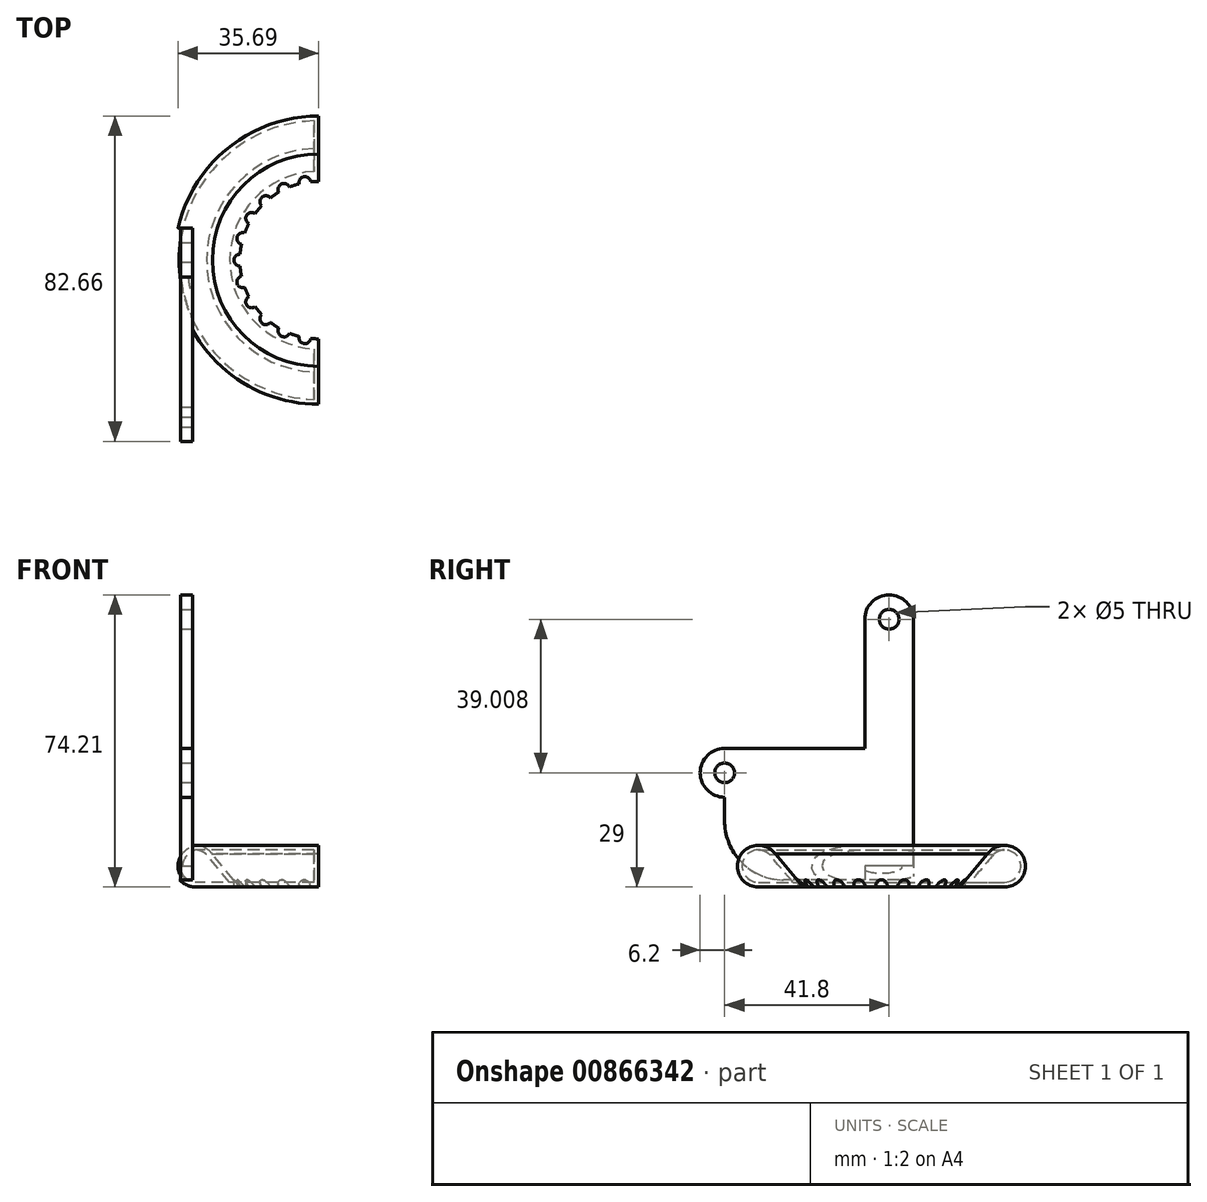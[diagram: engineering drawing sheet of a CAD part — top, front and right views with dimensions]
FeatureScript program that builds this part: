
annotation { "Feature Type Name" : "Feature", "Feature Type Description" : "" }
export const myFeature = defineFeature(function(context is Context, id is Id, definition is map)
    precondition{}
    {
        {
            var Q0;
            Q0=qCreatedBy(makeId("Front.planeOp"),FACE);
            var sketch = newSketch(context, id + "F0", { "sketchPlane" : qUnion([Q0])});
            skArc(sketch, "E0", {"start": v(-28.43, 2.91) * mm, "mid": v(-35.1, 1.56) * mm, "end": v(-31.3, -4.1) * mm});
            skLineSegment(sketch, "E1", {"start": v(-31.3, -4.1) * mm, "end": v(-31.3, -4.1) * mm});
            skLineSegment(sketch, "E2", {"start": v(-31.3, -4.1) * mm, "end": v(-22.57, -4.1) * mm});
            skLineSegment(sketch, "E3", {"start": v(-22.57, -4.1) * mm, "end": v(-28.43, 2.91) * mm});
            skArc(sketch, "E4.0", {"start": v(-26.94, 3) * mm, "mid": v(-36, 2.47) * mm, "end": v(-31.3, -5.3) * mm});
            skLineSegment(sketch, "E5.0", {"start": v(-20, -5.3) * mm, "end": v(-26.97, 3.05) * mm});
            skLineSegment(sketch, "E5.1", {"start": v(-31.3, -5.3) * mm, "end": v(-20, -5.3) * mm});
            skSolve(sketch);
        }
        {
            var Q0;
            Q0=qCreatedBy(makeId("Top.planeOp"),FACE);
            var sketch = newSketch(context, id + "F1", { "sketchPlane" : qUnion([Q0])});
            skCircle(sketch, "E6", {"center": v(0, 0) * mm, "radius": 20 * mm, "construction": true});
            skSolve(sketch);
        }
        {
            var Q0;
            {var subQ3=sQuery(id+"F0.wireOp",EDGE,"E2");Q0=makeQuery(id+"F0.imprint","IMPRINT",FACE,{"disambiguationData":[TD([[makeQuery(id+"F0.imprint","IMPRINT",EDGE,{"derivedFrom":subQ3}),-1.0]])]});}
            var Q1;
            Q1=sQuery(id+"F1.wireOp",EDGE,"E6");
            revolve(context, id + "F2", {"surfaceOperationType" : NewSurfaceOperationType.NEW, "entities" : qUnion([Q0]), "axis" : qUnion([Q1]), "revolveType" : RevolveType.SYMMETRIC, "angle" : 180 * degree});
        }
        {
            var Q0;
            Q0=qCreatedBy(makeId("Top.planeOp"),FACE);
            cPlane(context, id + "F3", {"entities" : qUnion([Q0]), "cplaneType" : CPlaneType.OFFSET, "offset" : 7 * mm, "width" : 150 * mm, "height" : 150 * mm});
        }
        {
            var Q0;
            Q0=qCreatedBy(id+"F3.planeOp",FACE);
            var sketch = newSketch(context, id + "F4", { "sketchPlane" : qUnion([Q0])});
            skCircle(sketch, "E7", {"center": v(-20.03, 0) * mm, "radius": 1.5 * mm});
            skSolve(sketch);
        }
        {
            var Q0;
            Q0=makeQuery(id+"F4.imprint","IMPRINT",FACE,{"disambiguationData":[TD([[makeQuery(id+"F4.imprint","IMPRINT",EDGE,{"derivedFrom":sQuery(id+"F4.wireOp",EDGE,"86y424w5-kA8f-6XOt-aXa2-UrsFHTbOcK4u")}),-1.0]])]});
            var Q1;
            Q1=makeQuery(id+"F4.imprint","IMPRINT",FACE,{"disambiguationData":[TD([[makeQuery(id+"F4.imprint","IMPRINT",EDGE,{"derivedFrom":sQuery(id+"F4.wireOp",EDGE,"E7")}),1.0]])]});
            var Q2;
            Q2=sQuery(id+"F4.wireOp",EDGE,"RAvej1WS-v9vJ-C49S-39A3-zDTatcSTJvx6");
            var Q3;
            Q3=sQuery(id+"F4.wireOp",EDGE,"86y424w5-kA8f-6XOt-aXa2-UrsFHTbOcK4u");
            var Q4;
            Q4=sQuery(id+"F4.wireOp",EDGE,"Bvj7dinE-6FqB-1OQW-Px6F-VovOO4BtMCvj");
            var Q5;
            Q5=makeQuery(id+"F2.opRevolve","SWEPT_FACE",FACE,{"disambiguationData":[OSD([sQuery(id+"F0.wireOp",EDGE,"E5.1")])]});
            extrude(context, id + "F5", {"entities" : qUnion([Q0, Q1]), "surfaceEntities" : qUnion([Q2, Q3, Q4]), "oppositeDirection" : true, "depth" : 20 * mm, "endBoundEntityFace" : qUnion([Q5]), "offsetDistance" : 25 * mm, "hasDraft" : true, "draftAngle" : 0 * degree});
        }
        {
            var Q0;
            Q0=makeQuery(id+"F5.opExtrude","SWEPT_BODY",BODY,{"disambiguationData":[OSD([sQuery(id+"F4.wireOp",EDGE,"E7")])]});
            var Q1;
            Q1=makeQuery(id+"F2.opRevolve","SWEPT_FACE",FACE,{"disambiguationData":[OSD([sQuery(id+"F0.wireOp",EDGE,"E5.0")])]});
            circularPattern(context, id + "F6", {"operationType" : NewBodyOperationType.REMOVE, "entities" : qUnion([Q0]), "axis" : qUnion([Q1]), "angle" : 160 * degree, "instanceCount" : 11, "equalSpace" : true, "isCentered" : true});
        }
        {
            var Q0;
            Q0=qCreatedBy(makeId("Right.planeOp"),FACE);
            var sketch = newSketch(context, id + "F7", { "sketchPlane" : qUnion([Q0])});
            skArc(sketch, "E8", {"start": v(-28.43, 2.91) * mm, "mid": v(-35.1, 1.56) * mm, "end": v(-31.3, -4.1) * mm});
            skLineSegment(sketch, "E9", {"start": v(-31.3, -4.1) * mm, "end": v(-31.3, -4.1) * mm});
            skLineSegment(sketch, "E10", {"start": v(-31.3, -4.1) * mm, "end": v(-22.57, -4.1) * mm});
            skLineSegment(sketch, "E11", {"start": v(-22.57, -4.1) * mm, "end": v(-28.43, 2.91) * mm});
            skArc(sketch, "E12.0", {"start": v(-26.94, 3) * mm, "mid": v(-36, 2.47) * mm, "end": v(-31.3, -5.3) * mm});
            skLineSegment(sketch, "E13.0", {"start": v(-20, -5.3) * mm, "end": v(-26.97, 3.05) * mm});
            skLineSegment(sketch, "E13.1", {"start": v(-31.3, -5.3) * mm, "end": v(-20, -5.3) * mm});
            skArc(sketch, "E14.MirrorCS", {"start": v(28.43, 2.91) * mm, "mid": v(35.1, 1.56) * mm, "end": v(31.3, -4.1) * mm});
            skArc(sketch, "E15.MirrorCS", {"start": v(26.94, 3) * mm, "mid": v(36, 2.47) * mm, "end": v(31.3, -5.3) * mm});
            skLineSegment(sketch, "E16.MirrorCS", {"start": v(22.57, -4.1) * mm, "end": v(28.43, 2.91) * mm});
            skLineSegment(sketch, "E17.MirrorCS", {"start": v(20, -5.3) * mm, "end": v(26.97, 3.05) * mm});
            skLineSegment(sketch, "E18.MirrorCS", {"start": v(31.3, -4.1) * mm, "end": v(22.57, -4.1) * mm});
            skLineSegment(sketch, "E19.MirrorCS", {"start": v(31.3, -5.3) * mm, "end": v(20, -5.3) * mm});
            skSolve(sketch);
        }
        {
            var Q0;
            Q0=makeQuery(id+"F7.imprint","IMPRINT",FACE,{"disambiguationData":[TD([[makeQuery(id+"F7.imprint","IMPRINT",EDGE,{"derivedFrom":sQuery(id+"F7.wireOp",EDGE,"E8")}),1.0]])]});
            var Q1;
            Q1=makeQuery(id+"F7.imprint","IMPRINT",FACE,{"disambiguationData":[TD([[makeQuery(id+"F7.imprint","IMPRINT",EDGE,{"derivedFrom":sQuery(id+"F7.wireOp",EDGE,"E8")}),-1.0]])]});
            extrude(context, id + "F8", {"entities" : qUnion([Q0, Q1]), "operationType" : NewBodyOperationType.ADD, "oppositeDirection" : true, "depth" : 1.2 * mm, "offsetDistance" : 25 * mm});
        }
        {
            var Q0;
            Q0=makeQuery(id+"F7.imprint","IMPRINT",FACE,{"disambiguationData":[TD([[makeQuery(id+"F7.imprint","IMPRINT",EDGE,{"derivedFrom":sQuery(id+"F7.wireOp",EDGE,"E14.MirrorCS")}),-1.0]])]});
            var Q1;
            Q1=makeQuery(id+"F7.imprint","IMPRINT",FACE,{"disambiguationData":[TD([[makeQuery(id+"F7.imprint","IMPRINT",EDGE,{"derivedFrom":sQuery(id+"F7.wireOp",EDGE,"E14.MirrorCS")}),1.0]])]});
            extrude(context, id + "F9", {"entities" : qUnion([Q0, Q1]), "operationType" : NewBodyOperationType.ADD, "oppositeDirection" : true, "depth" : 1.2 * mm, "offsetDistance" : 25 * mm});
        }
        {
            var Q0;
            Q0=qCreatedBy(makeId("Right.planeOp"),FACE);
            cPlane(context, id + "F10", {"entities" : qUnion([Q0]), "cplaneType" : CPlaneType.OFFSET, "offset" : 32 * mm, "oppositeDirection" : true, "width" : 150 * mm, "height" : 150 * mm});
        }
        {
            var Q0;
            Q0=qCreatedBy(id+"F10.planeOp",FACE);
            var sketch = newSketch(context, id + "F11", { "sketchPlane" : qUnion([Q0])});
            skLineSegment(sketch, "E20.bottom", {"start": v(8.15, 0) * mm, "end": v(-4.25, 0) * mm});
            skLineSegment(sketch, "E20.left", {"start": v(8.15, 0) * mm, "end": v(8.15, 62.7) * mm});
            skLineSegment(sketch, "E20.right", {"start": v(-4.25, 0) * mm, "end": v(-4.25, 62.7) * mm});
            skArc(sketch, "E21", {"start": v(8.15, 62.7) * mm, "mid": v(1.95, 68.9) * mm, "end": v(-4.25, 62.7) * mm});
            skSolve(sketch);
        }
        {
            var Q0;
            Q0 = qSketchRegion(id + "F11", true);
            extrude(context, id + "F12", {"entities" : qUnion([Q0]), "operationType" : NewBodyOperationType.ADD, "oppositeDirection" : true, "depth" : 3 * mm, "offsetDistance" : 25 * mm});
        }
        {
            var Q0;
            Q0=sQuery(id+"F11.wireOp",VERTEX,"E21.center");
            var Q1;
            Q1=makeQuery(id+"F2.opRevolve","SWEPT_BODY",BODY,{"disambiguationData":[OSD([sQuery(id+"F0.wireOp",EDGE,"E0"),sQuery(id+"F0.wireOp",EDGE,"E2"),sQuery(id+"F0.wireOp",EDGE,"E3"),sQuery(id+"F0.wireOp",EDGE,"E4.0"),sQuery(id+"F0.wireOp",EDGE,"E5.0"),sQuery(id+"F0.wireOp",EDGE,"E5.1")])]});
            hole(context, id + "F13", {"style" : HoleStyle.SIMPLE, "endStyle" : HoleEndStyle.THROUGH, "holeDiameter" : 5 * mm, "majorDiameter" : 5 * mm, "isTappedThrough" : true, "tappedDepth" : 12 * mm, "tapClearance" : 3, "startFromSketch" : true, "locations" : qUnion([Q0]), "scope" : qUnion([Q1])});
        }
        {
            var Q0;
            Q0=qCreatedBy(id+"F10.planeOp",FACE);
            var sketch = newSketch(context, id + "F14", { "sketchPlane" : qUnion([Q0])});
            skLineSegment(sketch, "E22", {"start": v(54.55, 23.7) * mm, "end": v(-64.28, 23.7) * mm, "construction": true});
            skLineSegment(sketch, "E23.bottom", {"start": v(-39.85, 29.9) * mm, "end": v(-4.25, 29.9) * mm});
            skLineSegment(sketch, "E23.top", {"start": v(-39.85, 17.5) * mm, "end": v(-4.25, 17.5) * mm});
            skLineSegment(sketch, "E23.right", {"start": v(-4.25, 29.9) * mm, "end": v(-4.25, 17.5) * mm});
            skArc(sketch, "E24", {"start": v(-39.85, 29.9) * mm, "mid": v(-46.05, 23.7) * mm, "end": v(-39.85, 17.5) * mm});
            skLineSegment(sketch, "E25.bottom", {"start": v(-4.25, 17.5) * mm, "end": v(-39.84, 17.5) * mm});
            skLineSegment(sketch, "E25.top", {"start": v(-4.25, -3.5) * mm, "end": v(-24.84, -3.5) * mm});
            skLineSegment(sketch, "E25.left", {"start": v(-4.25, 17.5) * mm, "end": v(-4.25, -3.5) * mm});
            skLineSegment(sketch, "E25.right", {"start": v(-39.84, 17.5) * mm, "end": v(-39.84, 11.5) * mm});
            skPoint(sketch, "E26.visualSharp", {"position": v(-39.84, -3.5) * mm});
            skArc(sketch, "E26.filletArc", {"start": v(-39.84, 11.5) * mm, "mid": v(-35.45, 0.9) * mm, "end": v(-24.84, -3.5) * mm});
            skSolve(sketch);
        }
        {
            var Q0;
            Q0 = qSketchRegion(id + "F14", true);
            extrude(context, id + "F15", {"entities" : qUnion([Q0]), "operationType" : NewBodyOperationType.ADD, "oppositeDirection" : true, "depth" : 3 * mm, "offsetDistance" : 25 * mm});
        }
        {
            var Q0;
            Q0=sQuery(id+"F14.wireOp",VERTEX,"E24.center");
            var Q1;
            Q1=makeQuery(id+"F2.opRevolve","SWEPT_BODY",BODY,{"disambiguationData":[OSD([sQuery(id+"F0.wireOp",EDGE,"E0"),sQuery(id+"F0.wireOp",EDGE,"E2"),sQuery(id+"F0.wireOp",EDGE,"E3"),sQuery(id+"F0.wireOp",EDGE,"E4.0"),sQuery(id+"F0.wireOp",EDGE,"E5.0"),sQuery(id+"F0.wireOp",EDGE,"E5.1")])]});
            hole(context, id + "F16", {"style" : HoleStyle.SIMPLE, "endStyle" : HoleEndStyle.THROUGH, "holeDiameter" : 5 * mm, "majorDiameter" : 5 * mm, "isTappedThrough" : true, "tappedDepth" : 12 * mm, "tapClearance" : 3, "startFromSketch" : true, "locations" : qUnion([Q0]), "scope" : qUnion([Q1])});
        }
        {
            var Q0;
            Q0=qCreatedBy(makeId("Top.planeOp"),FACE);
            var sketch = newSketch(context, id + "F17", { "sketchPlane" : qUnion([Q0])});
            skLineSegment(sketch, "E27.bottom", {"start": v(-35, 8.15) * mm, "end": v(-51, 8.15) * mm});
            skLineSegment(sketch, "E27.top", {"start": v(-35, -13.85) * mm, "end": v(-51, -13.85) * mm});
            skLineSegment(sketch, "E27.left", {"start": v(-35, 8.15) * mm, "end": v(-35, -13.85) * mm});
            skLineSegment(sketch, "E27.right", {"start": v(-51, 8.15) * mm, "end": v(-51, -13.85) * mm});
            skLineSegment(sketch, "E28.0", {"start": v(-35, -12.65) * mm, "end": v(-49.8, -12.65) * mm});
            skLineSegment(sketch, "E28.1", {"start": v(-49.8, 6.95) * mm, "end": v(-49.8, -12.65) * mm});
            skLineSegment(sketch, "E28.2", {"start": v(-35, 6.95) * mm, "end": v(-49.8, 6.95) * mm});
            skSolve(sketch);
        }
        {
            var Q0;
            Q0=makeQuery(id+"F17.imprint","IMPRINT",FACE,{"disambiguationData":[TD([[makeQuery(id+"F17.imprint","IMPRINT",EDGE,{"derivedFrom":sQuery(id+"F17.wireOp",EDGE,"E27.bottom")}),1.0]])]});
            var Q1;
            {var subQ0=sQuery(id+"F17.wireOp",EDGE,"E28.0");Q1=makeQuery(id+"F17.imprint","IMPRINT",FACE,{"disambiguationData":[TD([[makeQuery(id+"F17.imprint","IMPRINT",EDGE,{"derivedFrom":subQ0}),-1.0]])]});}
            extrude(context, id + "F18", {"entities" : qUnion([Q0, Q1]), "operationType" : NewBodyOperationType.REMOVE, "depth" : 17.4 * mm, "offsetDistance" : 25 * mm, "hasSecondDirection" : true, "secondDirectionOppositeDirection" : true, "secondDirectionDepth" : 3.5 * mm});
        }
    });
